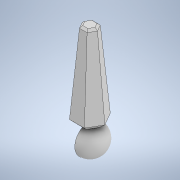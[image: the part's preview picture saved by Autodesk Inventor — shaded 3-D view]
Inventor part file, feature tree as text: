
AUTODESK INVENTOR PART (.ipt)
format: ipt  version: 2022 (Build 260153000, 153)  size: 154,624 bytes
history: native  units: in
note: dims shown in document units (in); Inventor stores cm internally (conversion verified against a paired STEP export)
features: sketch x5, revolve x2, sweep x1, hole x1
ambient origin geometry x8: Origin, YZ Plane, XZ Plane, XY Plane, X Axis, Y Axis, Z Axis, Center Point
bodies: Solid1 (feature_tree)
feature tree (9):
  sweep  "Sweep1"
  revolve  "Revolution2"  [1 undecoded]
  revolve  "Revolution3"  [1 undecoded]
  hole  "Hole1"  [1 undecoded]
  sketch  "Sketch1"  dims[d3=0.0in d4=0.0in d6=180.0deg]
  sketch  "Sketch2"  dims[d7=180.0deg]
  sketch  "Sketch3"  dims[d8=0.03in d9=0.75in d10=0.119in d11=0.25in d12=0.5635in d13=0.06in d14=0.0in d2=0.0344in]
  sketch  "Sketch4"  dims[d5=0.0344in]
  sketch  "Sketch5"
note: 3 required parameter values undecoded (feature->parameter linkage not recoverable at this tier; creation-order binding heuristic only, values carry confidence <= 0.55)